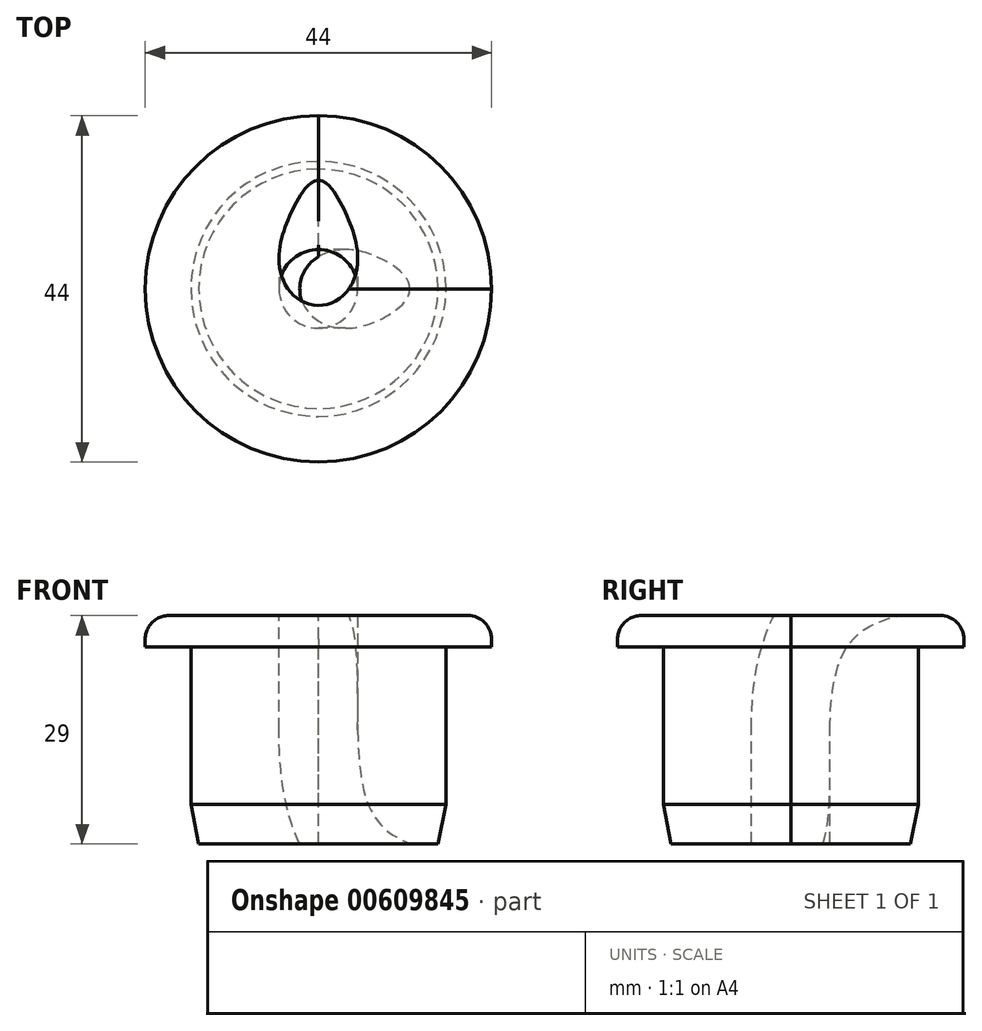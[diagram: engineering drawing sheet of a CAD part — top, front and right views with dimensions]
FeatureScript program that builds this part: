
annotation { "Feature Type Name" : "Feature", "Feature Type Description" : "" }
export const myFeature = defineFeature(function(context is Context, id is Id, definition is map)
    precondition{}
    {
        {
            var Q0;
            Q0=qCreatedBy(makeId("Front.planeOp"),FACE);
            var sketch = newSketch(context, id + "F0", { "sketchPlane" : qUnion([Q0])});
            skLineSegment(sketch, "E0.bottom", {"start": v(0, 0) * mm, "end": v(16.2, 0) * mm});
            skLineSegment(sketch, "E0.top", {"start": v(0, 29) * mm, "end": v(16.2, 29) * mm});
            skLineSegment(sketch, "E0.left", {"start": v(0, 0) * mm, "end": v(0, 29) * mm});
            skLineSegment(sketch, "E0.right", {"start": v(16.2, 0) * mm, "end": v(16.2, 29) * mm});
            skLineSegment(sketch, "E1.bottom", {"start": v(16.2, 29) * mm, "end": v(22, 29) * mm});
            skLineSegment(sketch, "E1.top", {"start": v(16.2, 25) * mm, "end": v(22, 25) * mm});
            skLineSegment(sketch, "E1.left", {"start": v(16.2, 29) * mm, "end": v(16.2, 25) * mm});
            skLineSegment(sketch, "E1.right", {"start": v(22, 29) * mm, "end": v(22, 25) * mm});
            skLineSegment(sketch, "E2", {"start": v(0, 46.92) * mm, "end": v(0, -27.4) * mm, "construction": true});
            skSolve(sketch);
        }
        {
            var Q0;
            Q0 = qSketchRegion(id + "F0", true);
            var Q1;
            Q1=sQuery(id+"F0.wireOp",EDGE,"E2");
            revolve(context, id + "F1", {"entities" : qUnion([Q0]), "axis" : qUnion([Q1]), "revolveType" : RevolveType.TWO_DIRECTIONS, "angle" : 270 * degree, "angleBack" : 0 * degree});
        }
        {
            var Q0;
            Q0=makeQuery(id+"F0.imprint","IMPRINT",FACE,{"disambiguationData":[TD([[makeQuery(id+"F0.imprint","IMPRINT",EDGE,{"derivedFrom":sQuery(id+"F0.wireOp",EDGE,"E0.bottom")}),1.0]])]});
            var Q1;
            Q1=makeQuery(id+"F0.imprint","IMPRINT",FACE,{"disambiguationData":[TD([[makeQuery(id+"F0.imprint","IMPRINT",EDGE,{"derivedFrom":sQuery(id+"F0.wireOp",EDGE,"E1.bottom")}),-1.0]])]});
            var Q2;
            Q2=sQuery(id+"F0.wireOp",EDGE,"E2");
            revolve(context, id + "F2", {"entities" : qUnion([Q0, Q1]), "axis" : qUnion([Q2]), "revolveType" : RevolveType.TWO_DIRECTIONS, "angle" : 360 * degree, "angleBack" : 270 * degree});
        }
        {
            var Q0;
            Q0=qCreatedBy(makeId("Front.planeOp"),FACE);
            var sketch = newSketch(context, id + "F3", { "sketchPlane" : qUnion([Q0])});
            skFitSpline(sketch, "E3", {"points": [v(0, 14.5) * mm, v(22.26, -7.83) * mm], "startDerivative": vector(0, -53.12) * mm, "endDerivative": vector(44.3, -8.62) * mm});
            skLineSegment(sketch, "E4", {"start": v(0, 29) * mm, "end": v(0, 0) * mm});
            skSolve(sketch);
        }
        {
            var Q0;
            Q0=qCreatedBy(makeId("Top.planeOp"),FACE);
            cPlane(context, id + "F4", {"entities" : qUnion([Q0]), "cplaneType" : CPlaneType.OFFSET, "offset" : 14.5 * mm, "width" : 150 * mm, "height" : 150 * mm});
        }
        {
            var Q0;
            Q0=qCreatedBy(id+"F4.planeOp",FACE);
            var sketch = newSketch(context, id + "F5", { "sketchPlane" : qUnion([Q0])});
            skCircle(sketch, "E5", {"center": v(0, 0) * mm, "radius": 5 * mm});
            skSolve(sketch);
        }
        {
            var Q0;
            Q0=makeQuery(id+"F5.imprint","IMPRINT",FACE,{"disambiguationData":[TD([[makeQuery(id+"F5.imprint","IMPRINT",EDGE,{"derivedFrom":sQuery(id+"F5.wireOp",EDGE,"E5")}),1.0]])]});
            var Q1;
            Q1=sQuery(id+"F3.wireOp",EDGE,"E3");
            sweep(context, id + "F6", {"operationType" : NewBodyOperationType.REMOVE, "profiles" : qUnion([Q0]), "path" : qUnion([Q1])});
        }
        {
            var Q0;
            Q0=makeQuery(id+"F5.imprint","IMPRINT",FACE,{"disambiguationData":[TD([[makeQuery(id+"F5.imprint","IMPRINT",EDGE,{"derivedFrom":sQuery(id+"F5.wireOp",EDGE,"E5")}),1.0]])]});
            var Q1;
            Q1=sQuery(id+"F3.wireOp",EDGE,"E3");
            sweep(context, id + "F7", {"operationType" : NewBodyOperationType.REMOVE, "profiles" : qUnion([Q0]), "path" : qUnion([Q1])});
        }
        {
            var Q0;
            Q0=qCreatedBy(makeId("Right.planeOp"),FACE);
            var sketch = newSketch(context, id + "F8", { "sketchPlane" : qUnion([Q0])});
            skFitSpline(sketch, "E6", {"points": [v(0, 14.5) * mm, v(24.4, 36.53) * mm], "startDerivative": vector(0, 63.61) * mm, "endDerivative": vector(35, 10.84) * mm});
            skSolve(sketch);
        }
        {
            var Q0;
            Q0=makeQuery(id+"F5.imprint","IMPRINT",FACE,{"disambiguationData":[TD([[makeQuery(id+"F5.imprint","IMPRINT",EDGE,{"derivedFrom":sQuery(id+"F5.wireOp",EDGE,"E5")}),1.0]])]});
            var Q1;
            Q1=sQuery(id+"F8.wireOp",EDGE,"E6");
            sweep(context, id + "F9", {"operationType" : NewBodyOperationType.REMOVE, "profiles" : qUnion([Q0]), "path" : qUnion([Q1])});
        }
        {
            var Q0;
            Q0=makeQuery(id+"F5.imprint","IMPRINT",FACE,{"disambiguationData":[TD([[makeQuery(id+"F5.imprint","IMPRINT",EDGE,{"derivedFrom":sQuery(id+"F5.wireOp",EDGE,"E5")}),1.0]])]});
            var Q1;
            Q1=sQuery(id+"F8.wireOp",EDGE,"E6");
            sweep(context, id + "F10", {"operationType" : NewBodyOperationType.REMOVE, "profiles" : qUnion([Q0]), "path" : qUnion([Q1])});
        }
        {
            var Q0;
            Q0=makeQuery(id+"F1.opRevolve","SWEPT_EDGE",EDGE,{"disambiguationData":[OSD([sQuery(id+"F0.wireOp",EDGE,"E1.bottom"),sQuery(id+"F0.wireOp",EDGE,"E1.right")])]});
            var Q1;
            Q1=makeQuery(id+"F2.opRevolve","SWEPT_EDGE",EDGE,{"disambiguationData":[OSD([sQuery(id+"F0.wireOp",EDGE,"E1.bottom"),sQuery(id+"F0.wireOp",EDGE,"E1.right")])]});
            fillet(context, id + "F11", {"entities" : qUnion([Q0, Q1]), "radius" : 3 * mm, "tangentPropagation" : true, "allowEdgeOverflow" : false});
        }
        {
            var Q0;
            Q0=makeQuery(id+"F1.opRevolve","SWEPT_EDGE",EDGE,{"disambiguationData":[OSD([sQuery(id+"F0.wireOp",EDGE,"E0.bottom"),sQuery(id+"F0.wireOp",EDGE,"E0.right")])]});
            var Q1;
            Q1=makeQuery(id+"F2.opRevolve","SWEPT_EDGE",EDGE,{"disambiguationData":[OSD([sQuery(id+"F0.wireOp",EDGE,"E0.bottom"),sQuery(id+"F0.wireOp",EDGE,"E0.right")])]});
            chamfer(context, id + "F12", {"entities" : qUnion([Q0, Q1]), "chamferType" : ChamferType.TWO_OFFSETS, "width1" : 5 * mm, "oppositeDirection" : false, "width2" : 1 * mm, "tangentPropagation" : true});
        }
    });
